SOLIDWORKS PART (.sldprt)
format: sldprt  version: not decoded by parser v0  size: 187,904 bytes
history: native  units: mm
features: sketch x17, extrude x7, revolve x4, plane x3, mirror x1, cut_extrude x1 (+7 scaffold rows collapsed)
feature tree (40):
  scaffold x7  (default folders/planes/origin — collapsed)
  plane  "front x-y"
  plane  "top y-z"
  plane  "side x-z"
  sketch  "Sketch1"  dims[D1=304.8mm D2=203.2mm]
  extrude  "Base-Extrude"  Depth=254mm
  sketch  "Sketch4"  dims[D1=25.4mm]
  extrude  "Boss-Extrude3"  Depth=50.8mm
  sketch  "Sketch5"
  sketch  "Sketch6"  dims[D1=25.4mm]
  revolve  "Boss-Revolve1"  Angle=180deg
  sketch  "Sketch7"  dims[D1=25.4mm D2=25.4mm]
  extrude  "Boss-Extrude4"  Depth=50.8mm
  sketch  "Sketch8"
  sketch  "Sketch9"  dims[D1=25.4mm]
  revolve  "Boss-Revolve2"  Angle=180deg
  mirror  "Mirror4"
  sketch  "Sketch10"
  sketch  "Sketch12"  dims[D1=0.0mm]
  extrude  "Boss-Extrude5"  Depth=203.2mm
  sketch  "Sketch13"
  cut_extrude  "Cut-Extrude1"  Depth=203.2mm
  sketch  "Sketch14"  dims[D1=25.4mm D2=25.4mm]
  extrude  "Boss-Extrude6"  Depth=50.8mm
  sketch  "Sketch15"
  sketch  "Sketch16"  dims[D1=25.4mm]
  revolve  "Boss-Revolve3"  Angle=180deg
  sketch  "Sketch17"  dims[D1=25.4mm D2=25.4mm]
  extrude  "Boss-Extrude7"  Depth=50.8mm
  sketch  "Sketch18"
  sketch  "Sketch19"  dims[D1=25.4mm]
  revolve  "Boss-Revolve4"  Angle=180deg
  sketch  "Sketch20"
  extrude  "Boss-Extrude8"  Depth=25.4mm
decode coverage: 22 of 30 modeling features carry decoded parameters
note: suppression state not decoded; provenance and decode notes live in map.json
